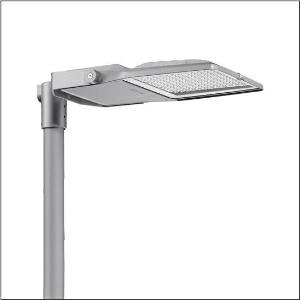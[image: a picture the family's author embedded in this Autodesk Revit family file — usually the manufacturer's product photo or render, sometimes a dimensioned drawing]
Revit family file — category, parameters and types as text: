
# Revit family: floodlight_fl_21_midi___pl43_5xa7786e2a3a_b253
name_source: partatom
category: Lighting Fixtures
units: mm (PartAtom-declared; Revit-internal decimal feet)

## family parameters
Cut with Voids When Loaded = No
Host = Face
Light Source = No
Part Type = Normal
Room Calculation Point = No
Round Connector Dimension = Use Diameter
Shared = No

## types (1)
- --- (1 x LED, 27640 lm, 212.4 W, 3000K)
    Apparent Load = 212 VA
    CIE Flux Codes = 27 78 99 100 100
    Color Rendering = 70
    Color Temperature = 3000K
    Default Elevation = 1800 mm
    Description = Floodlight FL 21 midi, floodlight, primary light control with lens, of PMMA, primary optical cover: protective disc, of toughened safety glass, transparent, light distribution: PL43, light emission: direct distribution, installation type: surface-mounted, LED, High Power LED, rated luminous flux: 27.640lm, luminous efficacy: 130lm/W, light colour: 730, colour temperature: 3000K, control gear: ECG Smart Interface, control: flexible luminous flux parameterisation, time-dependent luminous flux control, constant luminous flux control, overheat protection, presetting dimming logarithmic, with terminal, 6-pole, mains connection: 220..240V, AC, 50/60Hz, start of lifetime: 212W, end of service life: 231W, reduction: 95W, luminaire housing, of diecast aluminium, powder-coated, Siteco® metallic grey (DB 702S), corrosivity category C5 mid according to DIN EN ISO 12944, sealing non-destructively replaceable, please order mast flange separately, mast bracket, of steel, galvanised, powder-coated, Siteco® metallic grey (DB 702S), Smart Interface below and above, protection rating (complete): IP66, insulation class (complete): insulation class II (safety insulation), certification: CE, protection symbol: D, impact resistance: IK08, permissible operating ambient temperature: -40..+40°C, permissible operating ambient temperature for outdoor applications: -40..+50°C, standard: DIN EN 12944, LABS conformity tested according to VDMA 24364:2018-05, packaging unit: 1 piece

Light Distribution: PL43
    Height = 76 mm
    Lamp = 1 x LED
    Lamp Light Flux = 27640 lm
    Lamp Power = 212.4 W
    Lamp count = 1
    Length = 657 mm
    Luminous efficacy = 130 lm/W
    Manufacturer = Siteco
    ModVariant = No
    Model = 5XA7786E2A3A
    Number of Poles = 1
    OnlyDefault = Yes
    Power Factor = 1
    Product Name = Floodlight FL 21 midi | PL43
    Product group = floodlight | pylon annexe
    ProductGroupID = 6200
    Protection Class = Protection class II
    Protection Degree = IP 66
    RLX_Detail_Level = 1
    RLX_Emergency_Light_Flux = 0 lm
    RLX_Emergency_Type = 0
    RLX_Emergency_Type_DB = No
    RlxData = <blob elided: 153257 chars, md5=49898712>
    Socket = socket
    Standby Power = 0 W
    System Light Flux = 27640 lm
    System Power = 212 W
    Type Comments = factory setting: luminous flux: 100 % | dim-lin: 254 | 710 mA
    Type Image = l_1007123.jpg
    URL = http://relux.com
    VarID = @adj_128435
    Voltage = 0 V
    Weight = 0.00 kg
    Width = 442 mm

## geometry (parser evidence)
native form markers: Blend x4, Sweep x14
no freeform markers — native parametric forms only
